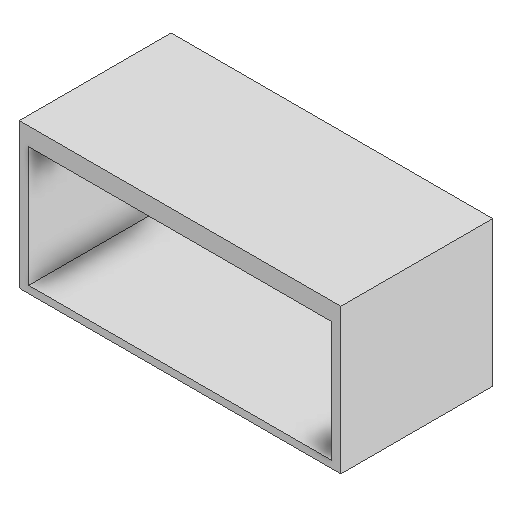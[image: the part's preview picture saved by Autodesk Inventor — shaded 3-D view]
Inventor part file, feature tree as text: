
AUTODESK INVENTOR PART (.ipt)
format: ipt  version: 2025.1 (Build 291241020, 241B)  size: 378,368 bytes
history: native  units: in
note: dims shown in document units (in); Inventor stores cm internally (conversion verified against a paired STEP export)
features: extrude x11, sketch x9, fillet x1, chamfer x1
ambient origin geometry x8: Origin, YZ Plane, XZ Plane, XY Plane, X Axis, Y Axis, Z Axis, Center Point
bodies: Solid1 (feature_tree)
feature tree (22):
  sketch  "Sketch1"  dims[d0=0.04in d1=3.2in d2=2.5in d3=0.6in d4=0.3in d5=0.5in d6=0.25in d7=0.085in d8=0.085in d9=0.085in d10=0.085in d11=0.1in d12=0.0in]
  extrude  "Extrusion1"  Depth=0.1in TaperAngle=0.0deg
  extrude  "Extrusion2"  Depth=0.1in TaperAngle=0.0deg
  extrude  "Extrusion4"  Depth=1.6in
  extrude  "Extrusion14"  Depth=2.5in
  extrude  "Extrusion15"  Depth=0.16in
  fillet  "Fillet1"  Radius=0.1834in
  extrude  "Extrusion16"  Depth=0.51in
  extrude  "Extrusion17"  Depth=0.5934in
  extrude  "Extrusion18"  Depth=0.25in
  extrude  "Extrusion19"  Depth=0.1in
  extrude  "Extrusion20"  Depth=2.0in
  extrude  "Extrusion21"  Depth=0.1in
  chamfer  "Chamfer3"  Distance=0.05in
  sketch  "Sketch9"  dims[d13=0.3in d14=0.0in d17=0.1in d18=0.0in]
  sketch  "Sketch10"  dims[d38=0.7in d40=1.6in]
  sketch  "Sketch11"  dims[d93=0.21in d94=2.5in]
  sketch  "Sketch12"  dims[d96=2.18in d97=0.16in d98=0.1834in]
  sketch  "Sketch13"  dims[d99=0.1in d100=0.51in]
  sketch  "Sketch14"  dims[d101=0.4934in d102=0.5934in]
  sketch  "Sketch15"  dims[d103=0.61in d104=0.25in]
  sketch  "Sketch16"  dims[d105=1.4in d106=0.1in d107=2.0in d108=0.2412in d109=0.05in d110=1.0499in d115=7.2in d116=0.75in d117=1.0in d118=0.0in d119=3.0in d120=1.0in d121=0.0in d122=1.5in d123=3.0in d124=0.4in d125=0.0in d126=6.65in d127=2.3in d129=0.2in d130=0.0in d131=0.21in d132=0.2in d133=0.0in d134=0.75in d135=0.8125in d136=0.0in d137=1.0in d138=0.8125in d139=0.0in d140=0.829in d141=0.2068in d142=0.1663in d143=0.1663in d144=0.2073in d145=0.2073in d146=0.2073in d147=0.2073in d148=0.1664in d149=0.8293in d150=0.8293in d151=1.0366in d152=0.2073in d153=0.2073in d154=0.2073in d155=0.1037in d156=0.207in d157=0.1in d158=0.0in d159=0.1in d160=0.125in d161=45.0deg]
